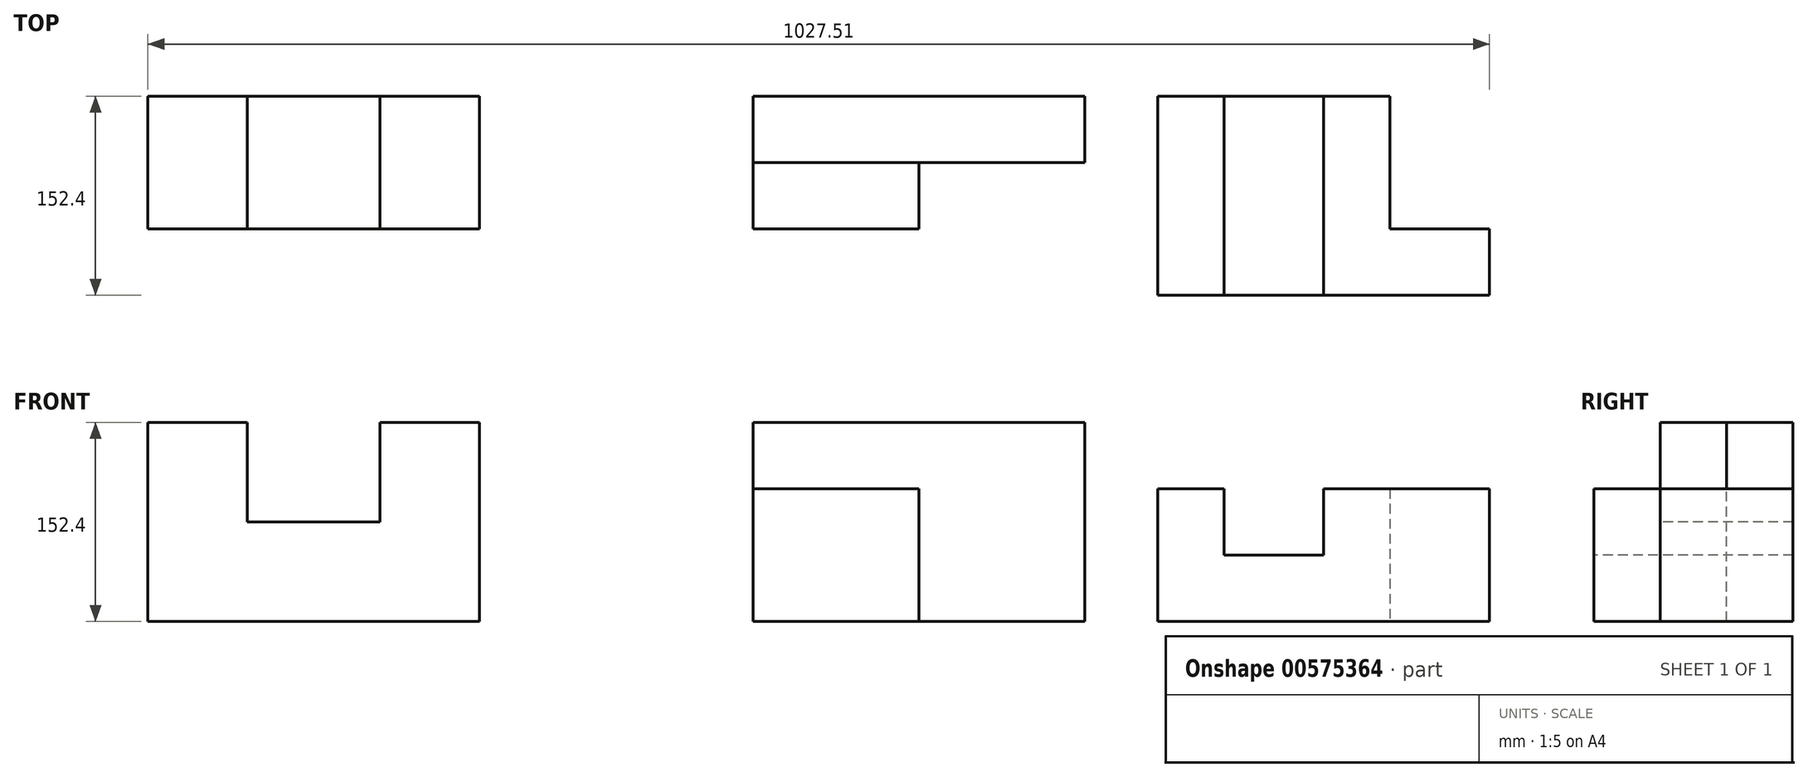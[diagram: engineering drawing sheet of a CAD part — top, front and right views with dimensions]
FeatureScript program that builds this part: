
annotation { "Feature Type Name" : "Feature", "Feature Type Description" : "" }
export const myFeature = defineFeature(function(context is Context, id is Id, definition is map)
    precondition{}
    {
        {
            var Q0;
            Q0=qCreatedBy(makeId("Front.planeOp"),FACE);
            var sketch = newSketch(context, id + "F0", { "sketchPlane" : qUnion([Q0])});
            skLineSegment(sketch, "E0", {"start": v(0, 0) * mm, "end": v(0, 152.4) * mm});
            skLineSegment(sketch, "E1", {"start": v(0, 152.4) * mm, "end": v(76.2, 152.4) * mm});
            skLineSegment(sketch, "E2", {"start": v(76.2, 152.4) * mm, "end": v(76.2, 76.2) * mm});
            skLineSegment(sketch, "E3", {"start": v(76.2, 76.2) * mm, "end": v(177.8, 76.2) * mm});
            skLineSegment(sketch, "E4", {"start": v(177.8, 76.2) * mm, "end": v(177.8, 152.4) * mm});
            skLineSegment(sketch, "E5", {"start": v(177.8, 152.4) * mm, "end": v(254, 152.4) * mm});
            skLineSegment(sketch, "E6", {"start": v(254, 152.4) * mm, "end": v(254, 0) * mm});
            skLineSegment(sketch, "E7", {"start": v(254, 0) * mm, "end": v(0, 0) * mm});
            skSolve(sketch);
        }
        {
            var Q0;
            Q0=makeQuery(id+"F0.imprint","IMPRINT",FACE,{"disambiguationData":[TD([[makeQuery(id+"F0.imprint","IMPRINT",EDGE,{"derivedFrom":sQuery(id+"F0.wireOp",EDGE,"E0")}),-1.0]])]});
            extrude(context, id + "F1", {"entities" : qUnion([Q0]), "oppositeDirection" : true, "depth" : 101.6 * mm, "offsetDistance" : 25.4 * mm});
        }
        {
            var Q0;
            Q0=qCreatedBy(makeId("Front.planeOp"),FACE);
            var sketch = newSketch(context, id + "F2", { "sketchPlane" : qUnion([Q0])});
            skLineSegment(sketch, "E8.bottom", {"start": v(463.57, 0) * mm, "end": v(717.57, 0) * mm});
            skLineSegment(sketch, "E8.top", {"start": v(463.57, 152.4) * mm, "end": v(717.57, 152.4) * mm});
            skLineSegment(sketch, "E8.left", {"start": v(463.57, 0) * mm, "end": v(463.57, 152.4) * mm});
            skLineSegment(sketch, "E8.right", {"start": v(717.57, 0) * mm, "end": v(717.57, 152.4) * mm});
            skSolve(sketch);
        }
        {
            var Q0;
            Q0=makeQuery(id+"F2.imprint","IMPRINT",FACE,{"disambiguationData":[TD([[makeQuery(id+"F2.imprint","IMPRINT",EDGE,{"derivedFrom":sQuery(id+"F2.wireOp",EDGE,"E8.bottom")}),1.0]])]});
            extrude(context, id + "F3", {"entities" : qUnion([Q0]), "oppositeDirection" : true, "depth" : 101.6 * mm, "offsetDistance" : 25.4 * mm});
        }
        {
            var Q0;
            Q0=makeQuery(id+"F3.opExtrude","SWEPT_FACE",FACE,{"disambiguationData":[OSD([sQuery(id+"F2.wireOp",EDGE,"E8.top")])]});
            var sketch = newSketch(context, id + "F4", { "sketchPlane" : qUnion([Q0])});
            skLineSegment(sketch, "E9.bottom", {"start": v(717.57, 0) * mm, "end": v(590.57, 0) * mm});
            skLineSegment(sketch, "E9.top", {"start": v(717.57, 50.8) * mm, "end": v(590.57, 50.8) * mm});
            skLineSegment(sketch, "E9.left", {"start": v(717.57, 0) * mm, "end": v(717.57, 50.8) * mm});
            skLineSegment(sketch, "E9.right", {"start": v(590.57, 0) * mm, "end": v(590.57, 50.8) * mm});
            skSolve(sketch);
        }
        {
            var Q0;
            Q0=makeQuery(id+"F4.imprint","IMPRINT",FACE,{"disambiguationData":[TD([[makeQuery(id+"F4.imprint","IMPRINT",EDGE,{"derivedFrom":sQuery(id+"F4.wireOp",EDGE,"E9.bottom")}),1.0]])]});
            extrude(context, id + "F5", {"entities" : qUnion([Q0]), "operationType" : NewBodyOperationType.REMOVE, "oppositeDirection" : true, "depth" : 152.4 * mm, "offsetDistance" : 25.4 * mm});
        }
        {
            var Q0;
            Q0=makeQuery(id+"F3.opExtrude","CAP_FACE",FACE,{"disambiguationData":[OSD([sQuery(id+"F2.wireOp",EDGE,"E8.bottom"),sQuery(id+"F2.wireOp",EDGE,"E8.top"),sQuery(id+"F2.wireOp",EDGE,"E8.left"),sQuery(id+"F2.wireOp",EDGE,"E8.right")])],"isStart":true});
            var sketch = newSketch(context, id + "F6", { "sketchPlane" : qUnion([Q0])});
            skLineSegment(sketch, "E10.bottom", {"start": v(463.57, 152.4) * mm, "end": v(590.57, 152.4) * mm});
            skLineSegment(sketch, "E10.top", {"start": v(463.57, 101.6) * mm, "end": v(590.57, 101.6) * mm});
            skLineSegment(sketch, "E10.left", {"start": v(463.57, 152.4) * mm, "end": v(463.57, 101.6) * mm});
            skLineSegment(sketch, "E10.right", {"start": v(590.57, 152.4) * mm, "end": v(590.57, 101.6) * mm});
            skSolve(sketch);
        }
        {
            var Q0;
            Q0=makeQuery(id+"F6.imprint","IMPRINT",FACE,{"disambiguationData":[TD([[makeQuery(id+"F6.imprint","IMPRINT",EDGE,{"derivedFrom":sQuery(id+"F6.wireOp",EDGE,"E10.bottom")}),-1.0]])]});
            extrude(context, id + "F7", {"entities" : qUnion([Q0]), "operationType" : NewBodyOperationType.REMOVE, "oppositeDirection" : true, "depth" : 50.8 * mm, "offsetDistance" : 25.4 * mm});
        }
        {
            var Q0;
            Q0=qCreatedBy(makeId("Front.planeOp"),FACE);
            var sketch = newSketch(context, id + "F8", { "sketchPlane" : qUnion([Q0])});
            skLineSegment(sketch, "E11", {"start": v(1102.77, 127) * mm, "end": v(1102.77, 76.2) * mm});
            skLineSegment(sketch, "E12", {"start": v(1102.77, 76.2) * mm, "end": v(1178.97, 76.2) * mm});
            skLineSegment(sketch, "E13", {"start": v(1178.97, 76.2) * mm, "end": v(1178.97, 0) * mm});
            skPoint(sketch, "E13.endSnap0", {"position": v(1204.98, 0) * mm});
            skLineSegment(sketch, "E14", {"start": v(1356.77, 0) * mm, "end": v(1356.77, 50.8) * mm});
            skLineSegment(sketch, "E15", {"start": v(1102.77, 127) * mm, "end": v(1280.57, 127) * mm});
            skLineSegment(sketch, "E16", {"start": v(1356.77, 0) * mm, "end": v(1178.97, 0) * mm});
            skLineSegment(sketch, "E17", {"start": v(1280.57, 127) * mm, "end": v(1280.57, 50.8) * mm});
            skLineSegment(sketch, "E18", {"start": v(1280.57, 50.8) * mm, "end": v(1356.77, 50.8) * mm});
            skSolve(sketch);
        }
        {
            var Q0;
            Q0=qCreatedBy(makeId("Top.planeOp"),FACE);
            var sketch = newSketch(context, id + "F9", { "sketchPlane" : qUnion([Q0])});
            skLineSegment(sketch, "E19", {"start": v(773.51, 0) * mm, "end": v(773.51, 101.6) * mm});
            skLineSegment(sketch, "E20", {"start": v(773.51, 101.6) * mm, "end": v(1027.51, 101.6) * mm});
            skLineSegment(sketch, "E21", {"start": v(1027.51, 101.6) * mm, "end": v(1027.51, 0) * mm});
            skLineSegment(sketch, "E22", {"start": v(773.51, 101.6) * mm, "end": v(824.31, 101.6) * mm});
            skLineSegment(sketch, "E23", {"start": v(824.31, 101.6) * mm, "end": v(824.31, 0) * mm});
            skLineSegment(sketch, "E24", {"start": v(900.51, 101.6) * mm, "end": v(900.51, 0) * mm});
            skLineSegment(sketch, "E25", {"start": v(951.31, 0) * mm, "end": v(951.31, 101.6) * mm});
            skLineSegment(sketch, "E26", {"start": v(951.31, 101.6) * mm, "end": v(951.31, 0) * mm});
            skLineSegment(sketch, "E27", {"start": v(773.51, 0) * mm, "end": v(773.51, -50.8) * mm});
            skLineSegment(sketch, "E28", {"start": v(773.51, -50.8) * mm, "end": v(1027.51, -50.8) * mm});
            skLineSegment(sketch, "E29", {"start": v(1027.51, -50.8) * mm, "end": v(1027.51, 0) * mm});
            skLineSegment(sketch, "E30", {"start": v(900.51, 0) * mm, "end": v(900.51, -50.8) * mm});
            skLineSegment(sketch, "E31", {"start": v(824.31, 0) * mm, "end": v(824.31, -50.8) * mm});
            skLineSegment(sketch, "E32", {"start": v(951.31, 0) * mm, "end": v(1027.51, 0) * mm});
            skSolve(sketch);
        }
        {
            var Q0;
            {var subQ4=sQuery(id+"F9.wireOp",EDGE,"E24");Q0=makeQuery(id+"F9.imprint","IMPRINT",FACE,{"disambiguationData":[TD([[makeQuery(id+"F9.imprint","IMPRINT",EDGE,{"derivedFrom":subQ4}),1.0]])]});}
            extrude(context, id + "F10", {"entities" : qUnion([Q0]), "depth" : 101.6 * mm, "offsetDistance" : 25.4 * mm});
        }
        {
            var Q0;
            {var subQ4=sQuery(id+"F9.wireOp",EDGE,"E23");Q0=makeQuery(id+"F9.imprint","IMPRINT",FACE,{"disambiguationData":[TD([[makeQuery(id+"F9.imprint","IMPRINT",EDGE,{"derivedFrom":subQ4}),1.0]])]});}
            extrude(context, id + "F11", {"entities" : qUnion([Q0]), "operationType" : NewBodyOperationType.ADD, "depth" : 50.8 * mm, "offsetDistance" : 25.4 * mm});
        }
        {
            var Q0;
            Q0=makeQuery(id+"F9.imprint","IMPRINT",FACE,{"disambiguationData":[TD([[makeQuery(id+"F9.imprint","IMPRINT",EDGE,{"derivedFrom":sQuery(id+"F9.wireOp",EDGE,"E19")}),-1.0]])]});
            extrude(context, id + "F12", {"entities" : qUnion([Q0]), "operationType" : NewBodyOperationType.ADD, "depth" : 101.6 * mm, "offsetDistance" : 25.4 * mm});
        }
    });
